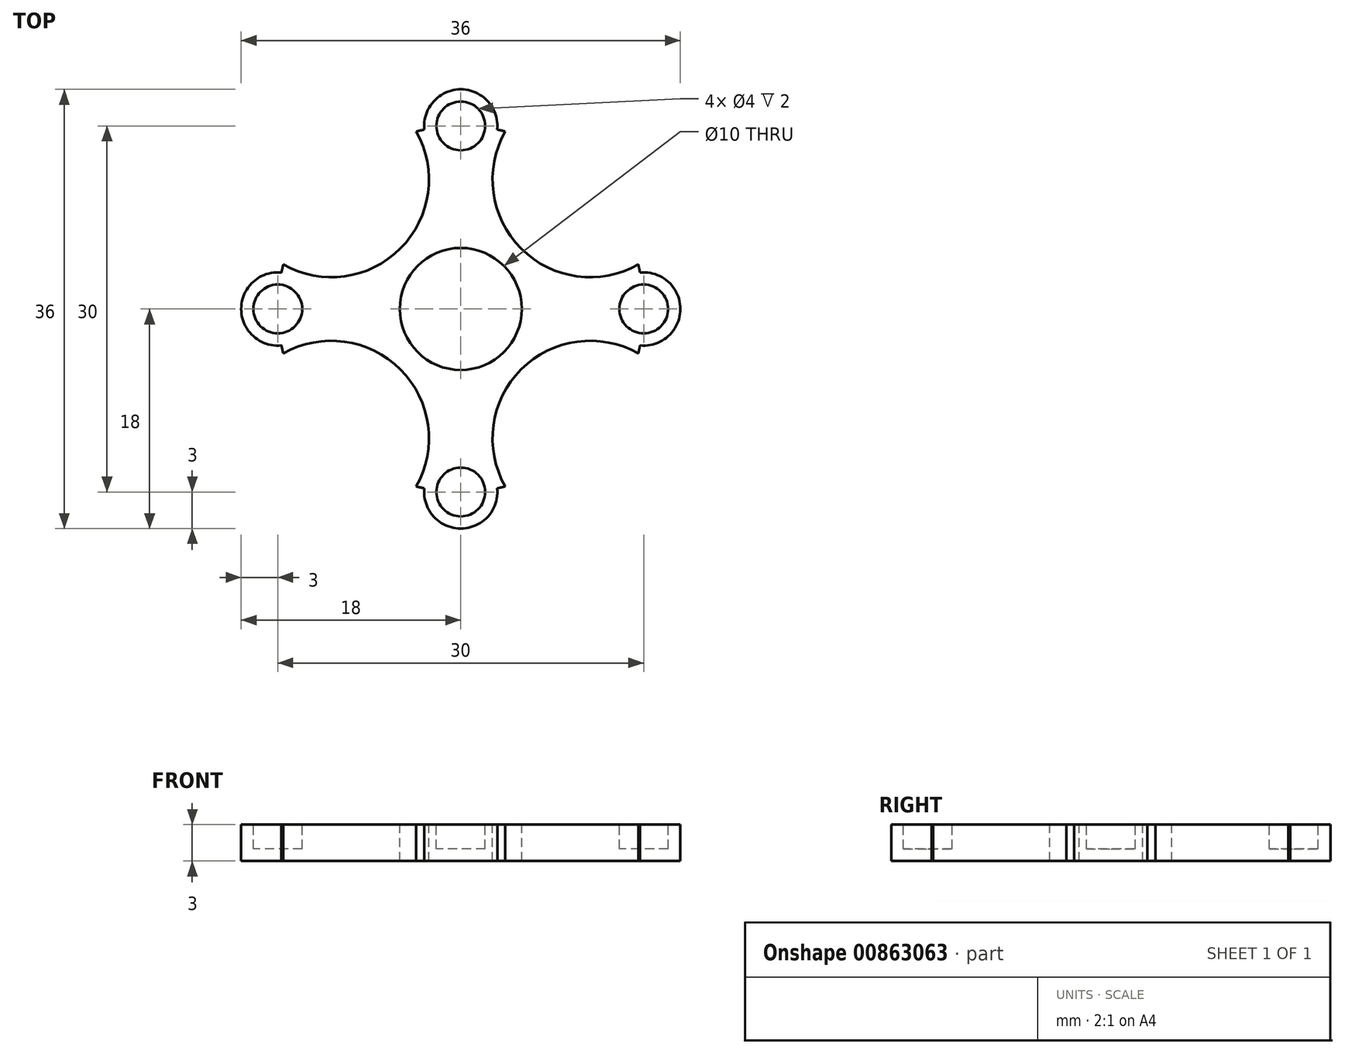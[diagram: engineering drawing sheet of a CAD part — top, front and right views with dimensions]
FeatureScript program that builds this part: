
annotation { "Feature Type Name" : "Feature", "Feature Type Description" : "" }
export const myFeature = defineFeature(function(context is Context, id is Id, definition is map)
    precondition{}
    {
        {
            var Q0;
            Q0=qCreatedBy(makeId("Top.planeOp"),FACE);
            var sketch = newSketch(context, id + "F0", { "sketchPlane" : qUnion([Q0])});
            skCircle(sketch, "E0", {"center": v(0, 0) * mm, "radius": 20 * mm});
            skSolve(sketch);
        }
        {
            var Q0;
            Q0=makeQuery(id+"F0.imprint","IMPRINT",FACE,{"disambiguationData":[TD([[makeQuery(id+"F0.imprint","IMPRINT",EDGE,{"derivedFrom":sQuery(id+"F0.wireOp",EDGE,"E0")}),1.0]])]});
            extrude(context, id + "F1", {"entities" : qUnion([Q0]), "depth" : 3 * mm, "offsetDistance" : 25 * mm});
        }
        {
            var Q0;
            Q0=makeQuery(id+"F1.opExtrude","CAP_FACE",FACE,{"disambiguationData":[OSD([sQuery(id+"F0.wireOp",EDGE,"E0")])],"isStart":false});
            var sketch = newSketch(context, id + "F2", { "sketchPlane" : qUnion([Q0])});
            skCircle(sketch, "E1", {"center": v(0, 0) * mm, "radius": 5 * mm});
            skSolve(sketch);
        }
        {
            var Q0;
            Q0=makeQuery(id+"F2.imprint","IMPRINT",FACE,{"disambiguationData":[TD([[makeQuery(id+"F2.imprint","IMPRINT",EDGE,{"derivedFrom":sQuery(id+"F2.wireOp",EDGE,"E1")}),1.0]])]});
            extrude(context, id + "F3", {"entities" : qUnion([Q0]), "operationType" : NewBodyOperationType.REMOVE, "oppositeDirection" : true, "depth" : 25 * mm, "offsetDistance" : 25 * mm});
        }
        {
            var Q0;
            Q0=makeQuery(id+"F1.opExtrude","CAP_FACE",FACE,{"disambiguationData":[OSD([sQuery(id+"F0.wireOp",EDGE,"E0")])],"isStart":false});
            var sketch = newSketch(context, id + "F4", { "sketchPlane" : qUnion([Q0])});
            skCircle(sketch, "E2", {"center": v(0, 15) * mm, "radius": 2 * mm});
            skCircle(sketch, "E3.1.0", {"center": v(-15, 0) * mm, "radius": 2 * mm});
            skCircle(sketch, "E3.2.0", {"center": v(0, -15) * mm, "radius": 2 * mm});
            skCircle(sketch, "E3.3.0", {"center": v(15, 0) * mm, "radius": 2 * mm});
            skPoint(sketch, "E3.center", {"position": v(0, 0) * mm});
            skSolve(sketch);
        }
        {
            var Q0;
            Q0=makeQuery(id+"F4.imprint","IMPRINT",FACE,{"disambiguationData":[TD([[makeQuery(id+"F4.imprint","IMPRINT",EDGE,{"derivedFrom":sQuery(id+"F4.wireOp",EDGE,"E2")}),1.0]])]});
            var Q1;
            Q1=makeQuery(id+"F4.imprint","IMPRINT",FACE,{"disambiguationData":[TD([[makeQuery(id+"F4.imprint","IMPRINT",EDGE,{"derivedFrom":sQuery(id+"F4.wireOp",EDGE,"E3.3.0")}),1.0]])]});
            var Q2;
            Q2=makeQuery(id+"F4.imprint","IMPRINT",FACE,{"disambiguationData":[TD([[makeQuery(id+"F4.imprint","IMPRINT",EDGE,{"derivedFrom":sQuery(id+"F4.wireOp",EDGE,"E3.2.0")}),1.0]])]});
            var Q3;
            Q3=makeQuery(id+"F4.imprint","IMPRINT",FACE,{"disambiguationData":[TD([[makeQuery(id+"F4.imprint","IMPRINT",EDGE,{"derivedFrom":sQuery(id+"F4.wireOp",EDGE,"E3.1.0")}),1.0]])]});
            extrude(context, id + "F5", {"entities" : qUnion([Q0, Q1, Q2, Q3]), "operationType" : NewBodyOperationType.REMOVE, "oppositeDirection" : true, "depth" : 2 * mm, "offsetDistance" : 25 * mm});
        }
        {
            var Q0;
            Q0=makeQuery(id+"F1.opExtrude","CAP_FACE",FACE,{"disambiguationData":[OSD([sQuery(id+"F0.wireOp",EDGE,"E0")])],"isStart":false});
            var sketch = newSketch(context, id + "F6", { "sketchPlane" : qUnion([Q0])});
            skLineSegment(sketch, "E4", {"start": v(0, 15) * mm, "end": v(-15, 0) * mm, "construction": true});
            skLineSegment(sketch, "E5", {"start": v(-7.5, 7.5) * mm, "end": v(11.18, -11.18) * mm, "construction": true});
            skLineSegment(sketch, "E6", {"start": v(-7.5, 7.5) * mm, "end": v(-14.14, 14.14) * mm, "construction": true});
            skCircle(sketch, "E7", {"center": v(-10.6, 10.6) * mm, "radius": 8 * mm});
            skCircle(sketch, "E8.1.0", {"center": v(-10.6, -10.6) * mm, "radius": 8 * mm});
            skCircle(sketch, "E8.2.0", {"center": v(10.6, -10.6) * mm, "radius": 8 * mm});
            skCircle(sketch, "E8.3.0", {"center": v(10.6, 10.6) * mm, "radius": 8 * mm});
            skPoint(sketch, "E8.center", {"position": v(0, 0) * mm});
            skSolve(sketch);
        }
        {
            var Q0;
            Q0=makeQuery(id+"F6.imprint","IMPRINT",FACE,{"disambiguationData":[TD([[makeQuery(id+"F6.imprint","IMPRINT",EDGE,{"derivedFrom":sQuery(id+"F6.wireOp",EDGE,"E7")}),1.0]])]});
            var Q1;
            Q1=makeQuery(id+"F6.imprint","IMPRINT",FACE,{"disambiguationData":[TD([[makeQuery(id+"F6.imprint","IMPRINT",EDGE,{"derivedFrom":sQuery(id+"F6.wireOp",EDGE,"E8.3.0")}),1.0]])]});
            var Q2;
            Q2=makeQuery(id+"F6.imprint","IMPRINT",FACE,{"disambiguationData":[TD([[makeQuery(id+"F6.imprint","IMPRINT",EDGE,{"derivedFrom":sQuery(id+"F6.wireOp",EDGE,"E8.2.0")}),1.0]])]});
            var Q3;
            Q3=makeQuery(id+"F6.imprint","IMPRINT",FACE,{"disambiguationData":[TD([[makeQuery(id+"F6.imprint","IMPRINT",EDGE,{"derivedFrom":sQuery(id+"F6.wireOp",EDGE,"E8.1.0")}),1.0]])]});
            extrude(context, id + "F7", {"entities" : qUnion([Q0, Q1, Q2, Q3]), "operationType" : NewBodyOperationType.REMOVE, "oppositeDirection" : true, "depth" : 25 * mm, "offsetDistance" : 25 * mm});
        }
        {
            var Q0;
            Q0=makeQuery(id+"F1.opExtrude","CAP_EDGE",EDGE,{"disambiguationData":[OSD([sQuery(id+"F0.wireOp",EDGE,"E0")])],"isStart":false});
            chamfer(context, id + "F8", {"entities" : qUnion([Q0]), "width" : 1.5 * mm, "tangentPropagation" : true});
        }
        {
            var Q0;
            Q0=makeQuery(id+"F1.opExtrude","CAP_FACE",FACE,{"disambiguationData":[OSD([sQuery(id+"F0.wireOp",EDGE,"E0")])],"isStart":false});
            var sketch = newSketch(context, id + "F9", { "sketchPlane" : qUnion([Q0])});
            skCircle(sketch, "E9", {"center": v(1.06, 0) * mm, "radius": 28.42 * mm});
            skArc(sketch, "E10", {"start": v(-14.7, 2.98) * mm, "mid": v(-18, 0) * mm, "end": v(-14.7, -2.98) * mm});
            skArc(sketch, "E11.1.0", {"start": v(-2.98, -14.7) * mm, "mid": v(0, -18) * mm, "end": v(2.98, -14.7) * mm});
            skArc(sketch, "E11.2.0", {"start": v(14.7, -2.98) * mm, "mid": v(18, 0) * mm, "end": v(14.7, 2.98) * mm});
            skArc(sketch, "E11.3.0", {"start": v(2.98, 14.7) * mm, "mid": v(0, 18) * mm, "end": v(-2.98, 14.7) * mm});
            skPoint(sketch, "E11.center", {"position": v(0, 0) * mm});
            skArc(sketch, "E12", {"start": v(-14.7, -2.98) * mm, "mid": v(-10.6, -10.6) * mm, "end": v(-2.98, -14.7) * mm});
            skArc(sketch, "E13.trimOffspring", {"start": v(2.98, -14.7) * mm, "mid": v(10.6, -10.6) * mm, "end": v(14.7, -2.98) * mm});
            skArc(sketch, "E14.trimOffspring", {"start": v(14.7, 2.98) * mm, "mid": v(10.6, 10.6) * mm, "end": v(2.98, 14.7) * mm});
            skArc(sketch, "E15.trimOffspring", {"start": v(-2.98, 14.7) * mm, "mid": v(-10.6, 10.6) * mm, "end": v(-14.7, 2.98) * mm});
            skSolve(sketch);
        }
        {
            var Q0;
            {var subQ6=sQuery(id+"F9.wireOp",EDGE,"E11.3.0");Q0=makeQuery(id+"F9.imprint","IMPRINT",FACE,{"disambiguationData":[TD([[makeQuery(id+"F9.imprint","IMPRINT",EDGE,{"derivedFrom":subQ6}),-1.0]])]});}
            var Q1;
            {var subQ1=sQuery(id+"F9.wireOp",EDGE,"E11.2.0");Q1=makeQuery(id+"F9.imprint","IMPRINT",FACE,{"disambiguationData":[TD([[makeQuery(id+"F9.imprint","IMPRINT",EDGE,{"derivedFrom":subQ1}),-1.0]])]});}
            var Q2;
            {var subQ5=sQuery(id+"F9.wireOp",EDGE,"E11.1.0");Q2=makeQuery(id+"F9.imprint","IMPRINT",FACE,{"disambiguationData":[TD([[makeQuery(id+"F9.imprint","IMPRINT",EDGE,{"derivedFrom":subQ5}),-1.0]])]});}
            var Q3;
            {var subQ6=sQuery(id+"F9.wireOp",EDGE,"E10");Q3=makeQuery(id+"F9.imprint","IMPRINT",FACE,{"disambiguationData":[TD([[makeQuery(id+"F9.imprint","IMPRINT",EDGE,{"derivedFrom":subQ6}),-1.0]])]});}
            var Q4;
            Q4=makeQuery(id+"F9.imprint","IMPRINT",FACE,{"disambiguationData":[TD([[makeQuery(id+"F9.imprint","IMPRINT",EDGE,{"derivedFrom":sQuery(id+"F9.wireOp",EDGE,"E9")}),1.0]])]});
            extrude(context, id + "F10", {"entities" : qUnion([Q0, Q1, Q2, Q3, Q4]), "operationType" : NewBodyOperationType.REMOVE, "oppositeDirection" : true, "depth" : 25 * mm, "offsetDistance" : 25 * mm});
        }
    });
